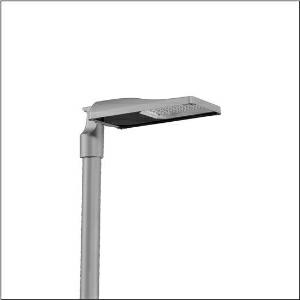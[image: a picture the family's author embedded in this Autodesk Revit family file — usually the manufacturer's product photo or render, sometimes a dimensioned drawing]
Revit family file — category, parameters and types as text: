
# Revit family: streetlight_sl_31_mini___st1_0a_5xh2d31b08ga_4c19
name_source: partatom
category: Lighting Fixtures
units: mm (PartAtom-declared; Revit-internal decimal feet)

## family parameters
Cut with Voids When Loaded = No
Host = Face
Light Source = No
Part Type = Normal
Room Calculation Point = No
Round Connector Dimension = Use Diameter
Shared = No

## types (1)
- --- (1 x LED, 5710 lm, 37.3 W, 3000K)
    Apparent Load = 37 VA
    CIE Flux Codes = 37 72 97 100 100
    Color Rendering = 70
    Color Temperature = 3000K
    Default Elevation = 1800 mm
    Description = Streetlight SL 31 mini Easy, LST, Desk-Remote mast luminaire for post-top, side-entry; light control with lens of PMMA; light distribution: ST1.0a, direct asymmetric distribution, for standard-compliant lighting for roads and squares; LED: luminous flux: 5.710lm, light colour: 730, colour temperature: 3000K; luminous efficacy: 153,1lm/W; control: pre-setting: linear dimming characteristic, flexible luminous flux parameterisation, time-dependent luminous flux control, constant luminous flux control, power reduction, intelligent temperature release in ECG and LED module, overheat protection; luminaire housing, of diecast aluminium, Siteco® metallic grey (DB 702S), corrosivity category C5 high according to DIN EN ISO 12944; cover of toughened safety glass, transparent, mast flange of diecast aluminium, Siteco® metallic grey (DB 702S), spigot size: 76/60mm, mast flange included unmounted; with cable H07RN-F 3x 1.5mm², cable length: 6,5m, connection cable pre-assembled; mains connection: 220..240V, AC, 50/60Hz; power consumption (at start of service life): 37,3W / (at end of service life): 38,7W / (with reduced operation 50%): 17,5W; protection rating (complete): IP66; insulation class (complete): insulation class II (safety insulation); impact resistance: IK10; certification: CE, ENEC, ENEC+, VDE, UKCA; permissible operating ambient temperature for outdoor applications: -40..+50°C; packaging unit: 1 piece

Light Distribution: ST1.0a
    Height = 76 mm
    Lamp = 1 x LED
    Lamp Light Flux = 5710 lm
    Lamp Power = 37.3 W
    Lamp count = 1
    Length = 547 mm
    Luminous efficacy = 153 lm/W
    Manufacturer = Siteco
    ModVariant = No
    Model = 5XH2D31B08GA
    Number of Poles = 1
    OnlyDefault = Yes
    Power Factor = 1
    Product Name = Streetlight SL 31 mini | ST1.0a
    Product group = mast luminaire | pylon top
    ProductGroupID = 6100
    Protection Class = Protection class II
    Protection Degree = IP 66
    RLX_Detail_Level = 1
    RLX_Emergency_Light_Flux = 0 lm
    RLX_Emergency_Type = 0
    RLX_Emergency_Type_DB = No
    RlxData = <blob elided: 39597 chars, md5=fb973d88>
    Socket = socket
    Standby Power = 0 W
    System Light Flux = 5710 lm
    System Power = 37 W
    Type Comments = factory setting: luminous flux: 100 % | dim-lin: 254 | 386 mA
    Type Image = l_1300326.jpg
    URL = http://relux.com
    VarID = @adj_055138
    Voltage = 0 V
    Weight = 0.00 kg
    Width = 265 mm

## geometry (parser evidence)
native form markers: Blend x4, Sweep x10
no freeform markers — native parametric forms only
